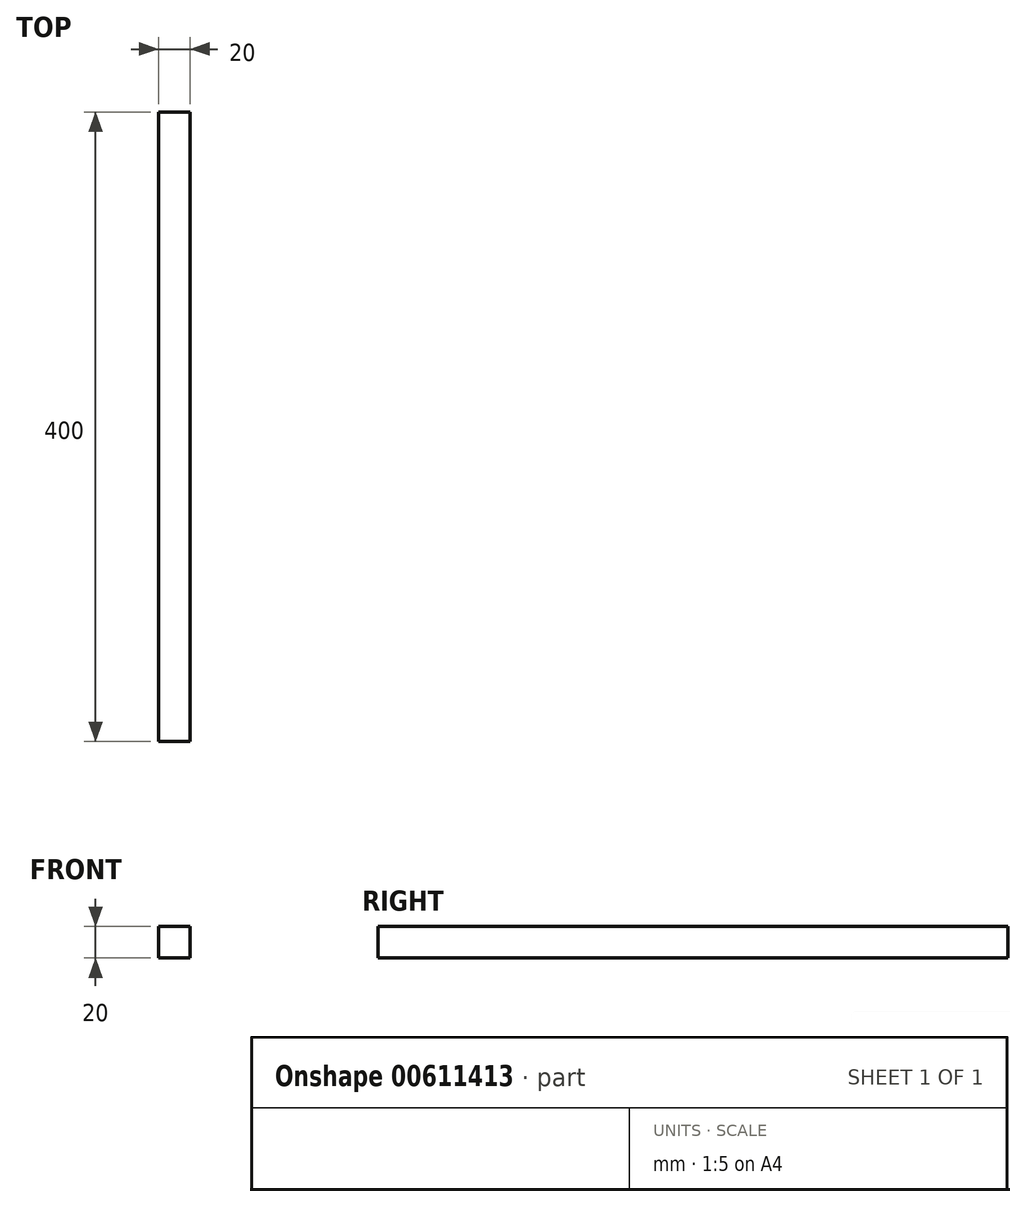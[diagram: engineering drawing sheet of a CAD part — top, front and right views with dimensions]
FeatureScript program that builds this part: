
annotation { "Feature Type Name" : "Feature", "Feature Type Description" : "" }
export const myFeature = defineFeature(function(context is Context, id is Id, definition is map)
    precondition{}
    {
        {
            var Q0;
            Q0=qCreatedBy(makeId("Front.planeOp"),FACE);
            var sketch = newSketch(context, id + "F0", { "sketchPlane" : qUnion([Q0])});
            skLineSegment(sketch, "E0.bottom", {"start": v(10, 10) * mm, "end": v(-10, 10) * mm});
            skLineSegment(sketch, "E0.top", {"start": v(10, -10) * mm, "end": v(-10, -10) * mm});
            skLineSegment(sketch, "E0.left", {"start": v(10, 10) * mm, "end": v(10, -10) * mm});
            skLineSegment(sketch, "E0.right", {"start": v(-10, 10) * mm, "end": v(-10, -10) * mm});
            skPoint(sketch, "E0.middle", {"position": v(0, 0) * mm});
            skSolve(sketch);
        }
        {
            var Q0;
            Q0=makeQuery(id+"F0.imprint","IMPRINT",FACE,{"disambiguationData":[TD([[makeQuery(id+"F0.imprint","IMPRINT",EDGE,{"derivedFrom":sQuery(id+"F0.wireOp",EDGE,"E0.bottom")}),1.0]])]});
            extrude(context, id + "F1", {"entities" : qUnion([Q0]), "depth" : 400 * mm, "offsetDistance" : 25 * mm});
        }
    });
